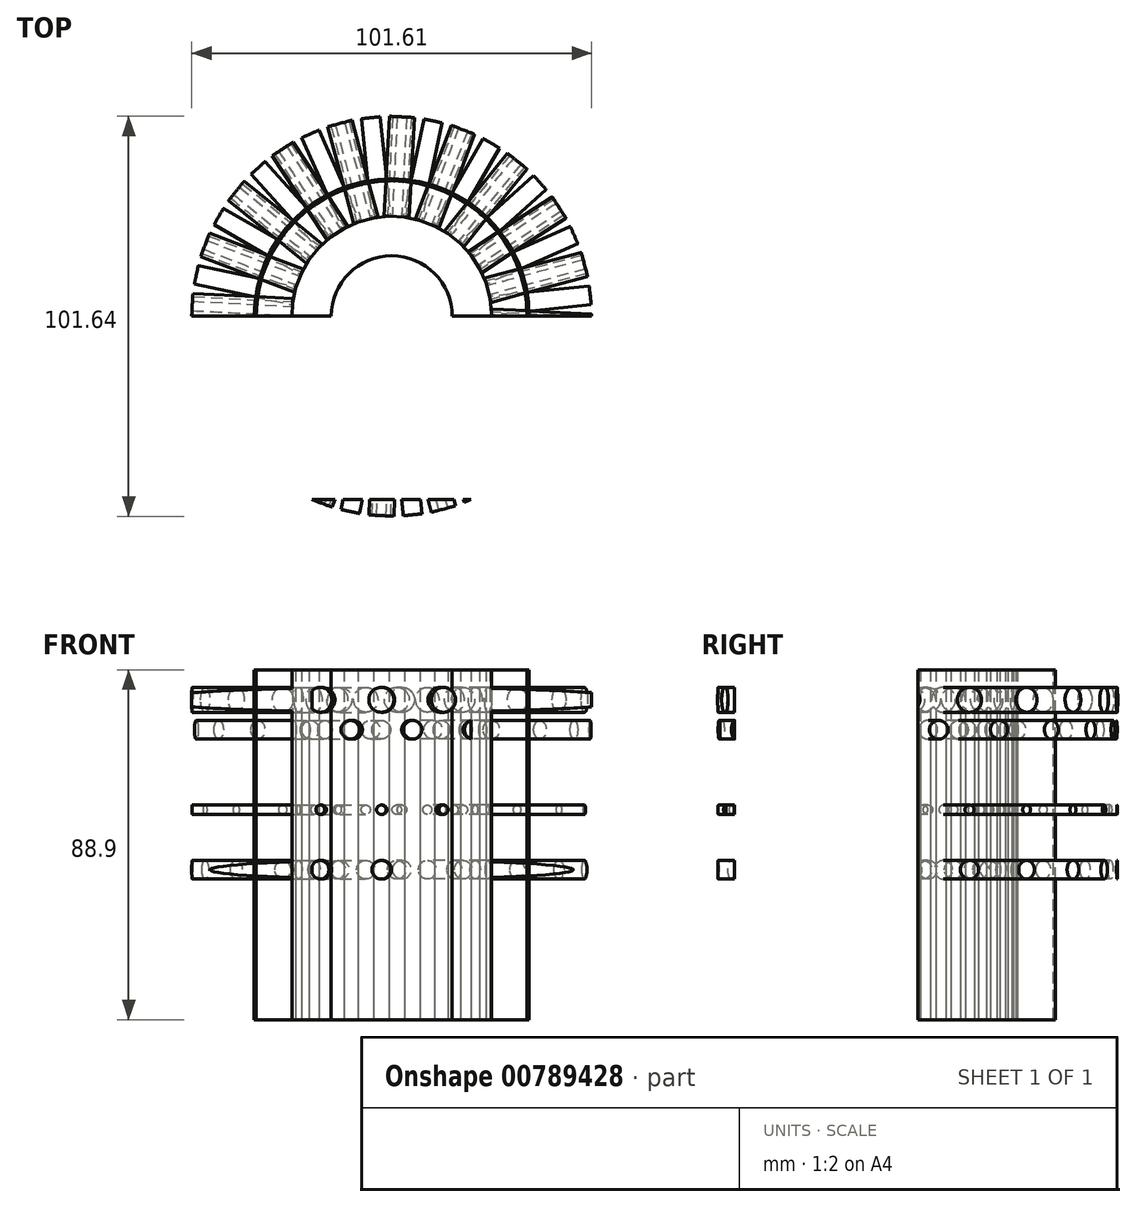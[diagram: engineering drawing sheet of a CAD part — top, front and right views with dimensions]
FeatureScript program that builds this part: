
annotation { "Feature Type Name" : "Feature", "Feature Type Description" : "" }
export const myFeature = defineFeature(function(context is Context, id is Id, definition is map)
    precondition{}
    {
        {
            var Q0;
            Q0=qCreatedBy(makeId("Top.planeOp"),FACE);
            var sketch = newSketch(context, id + "F0", { "sketchPlane" : qUnion([Q0])});
            skCircle(sketch, "E0.cCircle", {"center": v(0, 0) * mm, "radius": 25.32 * mm, "construction": true});
            skLineSegment(sketch, "E0.0", {"start": v(22.93, -10.92) * mm, "end": v(20.94, -14.37) * mm});
            skLineSegment(sketch, "E0.1", {"start": v(20.94, -14.37) * mm, "end": v(18.44, -17.47) * mm});
            skLineSegment(sketch, "E0.2", {"start": v(18.44, -17.47) * mm, "end": v(15.48, -20.14) * mm});
            skLineSegment(sketch, "E0.3", {"start": v(15.48, -20.14) * mm, "end": v(12.14, -22.31) * mm});
            skLineSegment(sketch, "E0.4", {"start": v(12.14, -22.31) * mm, "end": v(8.5, -23.94) * mm});
            skLineSegment(sketch, "E0.5", {"start": v(8.5, -23.94) * mm, "end": v(4.65, -24.97) * mm});
            skLineSegment(sketch, "E0.6", {"start": v(4.65, -24.97) * mm, "end": v(0.68, -25.4) * mm});
            skLineSegment(sketch, "E0.7", {"start": v(0.68, -25.4) * mm, "end": v(-3.3, -25.19) * mm});
            skLineSegment(sketch, "E0.8", {"start": v(-3.3, -25.19) * mm, "end": v(-7.2, -24.36) * mm});
            skLineSegment(sketch, "E0.9", {"start": v(-7.2, -24.36) * mm, "end": v(-10.92, -22.93) * mm});
            skLineSegment(sketch, "E0.10", {"start": v(-10.92, -22.93) * mm, "end": v(-14.37, -20.94) * mm});
            skLineSegment(sketch, "E0.11", {"start": v(-14.37, -20.94) * mm, "end": v(-17.47, -18.44) * mm});
            skLineSegment(sketch, "E0.12", {"start": v(-17.47, -18.44) * mm, "end": v(-20.14, -15.48) * mm});
            skLineSegment(sketch, "E0.13", {"start": v(-20.14, -15.48) * mm, "end": v(-22.31, -12.14) * mm});
            skLineSegment(sketch, "E0.14", {"start": v(-22.31, -12.14) * mm, "end": v(-23.94, -8.5) * mm});
            skLineSegment(sketch, "E0.15", {"start": v(-23.94, -8.5) * mm, "end": v(-24.97, -4.65) * mm});
            skLineSegment(sketch, "E0.16", {"start": v(-24.97, -4.65) * mm, "end": v(-25.4, -0.68) * mm});
            skLineSegment(sketch, "E0.17", {"start": v(-25.4, -0.68) * mm, "end": v(-25.19, 3.3) * mm});
            skLineSegment(sketch, "E0.18", {"start": v(-25.19, 3.3) * mm, "end": v(-24.36, 7.2) * mm});
            skLineSegment(sketch, "E0.19", {"start": v(-24.36, 7.2) * mm, "end": v(-22.93, 10.92) * mm});
            skLineSegment(sketch, "E0.20", {"start": v(-22.93, 10.92) * mm, "end": v(-20.94, 14.37) * mm});
            skLineSegment(sketch, "E0.21", {"start": v(-20.94, 14.37) * mm, "end": v(-18.44, 17.47) * mm});
            skLineSegment(sketch, "E0.22", {"start": v(-18.44, 17.47) * mm, "end": v(-15.48, 20.14) * mm});
            skLineSegment(sketch, "E0.23", {"start": v(-15.48, 20.14) * mm, "end": v(-12.14, 22.31) * mm});
            skLineSegment(sketch, "E0.24", {"start": v(-12.14, 22.31) * mm, "end": v(-8.5, 23.94) * mm});
            skLineSegment(sketch, "E0.25", {"start": v(-8.5, 23.94) * mm, "end": v(-4.65, 24.97) * mm});
            skLineSegment(sketch, "E0.26", {"start": v(-4.65, 24.97) * mm, "end": v(-0.68, 25.4) * mm});
            skLineSegment(sketch, "E0.27", {"start": v(-0.68, 25.4) * mm, "end": v(3.3, 25.19) * mm});
            skLineSegment(sketch, "E0.28", {"start": v(3.3, 25.19) * mm, "end": v(7.2, 24.36) * mm});
            skLineSegment(sketch, "E0.29", {"start": v(7.2, 24.36) * mm, "end": v(10.92, 22.93) * mm});
            skLineSegment(sketch, "E0.30", {"start": v(10.92, 22.93) * mm, "end": v(14.37, 20.94) * mm});
            skLineSegment(sketch, "E0.31", {"start": v(14.37, 20.94) * mm, "end": v(17.47, 18.44) * mm});
            skLineSegment(sketch, "E0.32", {"start": v(17.47, 18.44) * mm, "end": v(20.14, 15.48) * mm});
            skLineSegment(sketch, "E0.33", {"start": v(20.14, 15.48) * mm, "end": v(22.31, 12.14) * mm});
            skLineSegment(sketch, "E0.34", {"start": v(22.31, 12.14) * mm, "end": v(23.94, 8.5) * mm});
            skLineSegment(sketch, "E0.35", {"start": v(23.94, 8.5) * mm, "end": v(24.97, 4.65) * mm});
            skLineSegment(sketch, "E0.36", {"start": v(24.97, 4.65) * mm, "end": v(25.4, 0.68) * mm});
            skLineSegment(sketch, "E0.37", {"start": v(25.4, 0.68) * mm, "end": v(25.19, -3.3) * mm});
            skLineSegment(sketch, "E0.38", {"start": v(25.19, -3.3) * mm, "end": v(24.36, -7.2) * mm});
            skLineSegment(sketch, "E0.39", {"start": v(24.36, -7.2) * mm, "end": v(22.93, -10.92) * mm});
            skPoint(sketch, "E0.0.midPoint", {"position": v(21.94, -12.64) * mm});
            skCircle(sketch, "E1", {"center": v(0, 0) * mm, "radius": 15.37 * mm});
            skSolve(sketch);
        }
        {
            var Q0;
            Q0 = qSketchRegion(id + "F0", true);
            extrude(context, id + "F1", {"entities" : qUnion([Q0]), "depth" : 88.9 * mm, "offsetDistance" : 25.4 * mm});
        }
        {
            var Q0;
            Q0=makeQuery(id+"F1.opExtrude","SWEPT_FACE",FACE,{"disambiguationData":[OSD([sQuery(id+"F0.wireOp",EDGE,"E0.7")])]});
            var sketch = newSketch(context, id + "F2", { "sketchPlane" : qUnion([Q0])});
            skCircle(sketch, "E2", {"center": v(0, 81.28) * mm, "radius": 3.18 * mm});
            skPoint(sketch, "E2.centerSnap0", {"position": v(0, 88.9) * mm});
            skSolve(sketch);
        }
        {
            var Q0;
            Q0 = qSketchRegion(id + "F2", true);
            extrude(context, id + "F3", {"entities" : qUnion([Q0]), "depth" : 25.4 * mm, "offsetDistance" : 25.4 * mm});
        }
        {
            var Q0;
            Q0=makeQuery(id+"F3.opExtrude","SWEPT_BODY",BODY,{"disambiguationData":[OSD([sQuery(id+"F2.wireOp",EDGE,"E2")])]});
            var Q1;
            Q1=makeQuery(id+"F1.opExtrude","CAP_EDGE",EDGE,{"disambiguationData":[OSD([sQuery(id+"F0.wireOp",EDGE,"E1")])],"isStart":false});
            circularPattern(context, id + "F4", {"entities" : qUnion([Q0]), "axis" : qUnion([Q1]), "angle" : 360 * degree, "instanceCount" : 20, "equalSpace" : true});
        }
        {
            var Q0;
            Q0=makeQuery(id+"F4.opPattern","COPY",BODY,{"derivedFrom":makeQuery(id+"F3.opExtrude","SWEPT_BODY",BODY,{"disambiguationData":[OSD([sQuery(id+"F2.wireOp",EDGE,"E2")])]}),"instanceName":"10"});
            var Q1;
            Q1=makeQuery(id+"F4.opPattern","COPY",BODY,{"derivedFrom":makeQuery(id+"F3.opExtrude","SWEPT_BODY",BODY,{"disambiguationData":[OSD([sQuery(id+"F2.wireOp",EDGE,"E2")])]}),"instanceName":"11"});
            var Q2;
            Q2=makeQuery(id+"F4.opPattern","COPY",BODY,{"derivedFrom":makeQuery(id+"F3.opExtrude","SWEPT_BODY",BODY,{"disambiguationData":[OSD([sQuery(id+"F2.wireOp",EDGE,"E2")])]}),"instanceName":"12"});
            var Q3;
            Q3=makeQuery(id+"F4.opPattern","COPY",BODY,{"derivedFrom":makeQuery(id+"F3.opExtrude","SWEPT_BODY",BODY,{"disambiguationData":[OSD([sQuery(id+"F2.wireOp",EDGE,"E2")])]}),"instanceName":"13"});
            var Q4;
            Q4=makeQuery(id+"F4.opPattern","COPY",BODY,{"derivedFrom":makeQuery(id+"F3.opExtrude","SWEPT_BODY",BODY,{"disambiguationData":[OSD([sQuery(id+"F2.wireOp",EDGE,"E2")])]}),"instanceName":"14"});
            var Q5;
            Q5=makeQuery(id+"F4.opPattern","COPY",BODY,{"derivedFrom":makeQuery(id+"F3.opExtrude","SWEPT_BODY",BODY,{"disambiguationData":[OSD([sQuery(id+"F2.wireOp",EDGE,"E2")])]}),"instanceName":"15"});
            var Q6;
            Q6=makeQuery(id+"F4.opPattern","COPY",BODY,{"derivedFrom":makeQuery(id+"F3.opExtrude","SWEPT_BODY",BODY,{"disambiguationData":[OSD([sQuery(id+"F2.wireOp",EDGE,"E2")])]}),"instanceName":"16"});
            var Q7;
            Q7=makeQuery(id+"F4.opPattern","COPY",BODY,{"derivedFrom":makeQuery(id+"F3.opExtrude","SWEPT_BODY",BODY,{"disambiguationData":[OSD([sQuery(id+"F2.wireOp",EDGE,"E2")])]}),"instanceName":"17"});
            var Q8;
            Q8=makeQuery(id+"F4.opPattern","COPY",BODY,{"derivedFrom":makeQuery(id+"F3.opExtrude","SWEPT_BODY",BODY,{"disambiguationData":[OSD([sQuery(id+"F2.wireOp",EDGE,"E2")])]}),"instanceName":"18"});
            var Q9;
            Q9=makeQuery(id+"F4.opPattern","COPY",BODY,{"derivedFrom":makeQuery(id+"F3.opExtrude","SWEPT_BODY",BODY,{"disambiguationData":[OSD([sQuery(id+"F2.wireOp",EDGE,"E2")])]}),"instanceName":"19"});
            var Q10;
            Q10=makeQuery(id+"F3.opExtrude","SWEPT_BODY",BODY,{"disambiguationData":[OSD([sQuery(id+"F2.wireOp",EDGE,"E2")])]});
            var Q11;
            Q11=makeQuery(id+"F4.opPattern","COPY",BODY,{"derivedFrom":makeQuery(id+"F3.opExtrude","SWEPT_BODY",BODY,{"disambiguationData":[OSD([sQuery(id+"F2.wireOp",EDGE,"E2")])]}),"instanceName":"1"});
            var Q12;
            Q12=makeQuery(id+"F4.opPattern","COPY",BODY,{"derivedFrom":makeQuery(id+"F3.opExtrude","SWEPT_BODY",BODY,{"disambiguationData":[OSD([sQuery(id+"F2.wireOp",EDGE,"E2")])]}),"instanceName":"2"});
            var Q13;
            Q13=makeQuery(id+"F4.opPattern","COPY",BODY,{"derivedFrom":makeQuery(id+"F3.opExtrude","SWEPT_BODY",BODY,{"disambiguationData":[OSD([sQuery(id+"F2.wireOp",EDGE,"E2")])]}),"instanceName":"3"});
            var Q14;
            Q14=makeQuery(id+"F4.opPattern","COPY",BODY,{"derivedFrom":makeQuery(id+"F3.opExtrude","SWEPT_BODY",BODY,{"disambiguationData":[OSD([sQuery(id+"F2.wireOp",EDGE,"E2")])]}),"instanceName":"4"});
            var Q15;
            Q15=makeQuery(id+"F4.opPattern","COPY",BODY,{"derivedFrom":makeQuery(id+"F3.opExtrude","SWEPT_BODY",BODY,{"disambiguationData":[OSD([sQuery(id+"F2.wireOp",EDGE,"E2")])]}),"instanceName":"5"});
            var Q16;
            Q16=makeQuery(id+"F4.opPattern","COPY",BODY,{"derivedFrom":makeQuery(id+"F3.opExtrude","SWEPT_BODY",BODY,{"disambiguationData":[OSD([sQuery(id+"F2.wireOp",EDGE,"E2")])]}),"instanceName":"6"});
            var Q17;
            Q17=makeQuery(id+"F4.opPattern","COPY",BODY,{"derivedFrom":makeQuery(id+"F3.opExtrude","SWEPT_BODY",BODY,{"disambiguationData":[OSD([sQuery(id+"F2.wireOp",EDGE,"E2")])]}),"instanceName":"7"});
            var Q18;
            Q18=makeQuery(id+"F4.opPattern","COPY",BODY,{"derivedFrom":makeQuery(id+"F3.opExtrude","SWEPT_BODY",BODY,{"disambiguationData":[OSD([sQuery(id+"F2.wireOp",EDGE,"E2")])]}),"instanceName":"8"});
            var Q19;
            Q19=makeQuery(id+"F4.opPattern","COPY",BODY,{"derivedFrom":makeQuery(id+"F3.opExtrude","SWEPT_BODY",BODY,{"disambiguationData":[OSD([sQuery(id+"F2.wireOp",EDGE,"E2")])]}),"instanceName":"9"});
            var Q20;
            Q20=makeQuery(id+"F1.opExtrude","SWEPT_BODY",BODY,{"disambiguationData":[OSD([sQuery(id+"F0.wireOp",EDGE,"E0.0"),sQuery(id+"F0.wireOp",EDGE,"E0.1"),sQuery(id+"F0.wireOp",EDGE,"E0.2"),sQuery(id+"F0.wireOp",EDGE,"E0.3"),sQuery(id+"F0.wireOp",EDGE,"E0.4"),sQuery(id+"F0.wireOp",EDGE,"E0.5"),sQuery(id+"F0.wireOp",EDGE,"E0.6"),sQuery(id+"F0.wireOp",EDGE,"E0.7"),sQuery(id+"F0.wireOp",EDGE,"E0.8"),sQuery(id+"F0.wireOp",EDGE,"E0.9"),sQuery(id+"F0.wireOp",EDGE,"E0.10"),sQuery(id+"F0.wireOp",EDGE,"E0.11"),sQuery(id+"F0.wireOp",EDGE,"E0.12"),sQuery(id+"F0.wireOp",EDGE,"E0.13"),sQuery(id+"F0.wireOp",EDGE,"E0.14"),sQuery(id+"F0.wireOp",EDGE,"E0.15"),sQuery(id+"F0.wireOp",EDGE,"E0.16"),sQuery(id+"F0.wireOp",EDGE,"E0.17"),sQuery(id+"F0.wireOp",EDGE,"E0.18"),sQuery(id+"F0.wireOp",EDGE,"E0.19"),sQuery(id+"F0.wireOp",EDGE,"E0.20"),sQuery(id+"F0.wireOp",EDGE,"E0.21"),sQuery(id+"F0.wireOp",EDGE,"E0.22"),sQuery(id+"F0.wireOp",EDGE,"E0.23"),sQuery(id+"F0.wireOp",EDGE,"E0.24"),sQuery(id+"F0.wireOp",EDGE,"E0.25"),sQuery(id+"F0.wireOp",EDGE,"E0.26"),sQuery(id+"F0.wireOp",EDGE,"E0.27"),sQuery(id+"F0.wireOp",EDGE,"E0.28"),sQuery(id+"F0.wireOp",EDGE,"E0.29"),sQuery(id+"F0.wireOp",EDGE,"E0.30"),sQuery(id+"F0.wireOp",EDGE,"E0.31"),sQuery(id+"F0.wireOp",EDGE,"E0.32"),sQuery(id+"F0.wireOp",EDGE,"E0.33"),sQuery(id+"F0.wireOp",EDGE,"E0.34"),sQuery(id+"F0.wireOp",EDGE,"E0.35"),sQuery(id+"F0.wireOp",EDGE,"E0.36"),sQuery(id+"F0.wireOp",EDGE,"E0.37"),sQuery(id+"F0.wireOp",EDGE,"E0.38"),sQuery(id+"F0.wireOp",EDGE,"E0.39"),sQuery(id+"F0.wireOp",EDGE,"E1")])]});
            booleanBodies(context, id + "F5", {"operationType" : BooleanOperationType.UNION, "tools" : qUnion([Q0, Q1, Q2, Q3, Q4, Q5, Q6, Q7, Q8, Q9, Q10, Q11, Q12, Q13, Q14, Q15, Q16, Q17, Q18, Q19, Q20])});
        }
        {
            var Q0;
            Q0=makeQuery(id+"F1.opExtrude","SWEPT_FACE",FACE,{"disambiguationData":[OSD([sQuery(id+"F0.wireOp",EDGE,"E0.6")])]});
            var sketch = newSketch(context, id + "F6", { "sketchPlane" : qUnion([Q0])});
            skCircle(sketch, "E3", {"center": v(0, 73.66) * mm, "radius": 2.38 * mm});
            skSolve(sketch);
        }
        {
            var Q0;
            Q0 = qSketchRegion(id + "F6", true);
            extrude(context, id + "F7", {"entities" : qUnion([Q0]), "operationType" : NewBodyOperationType.ADD, "depth" : 25.4 * mm, "offsetDistance" : 25.4 * mm});
        }
        {
            var Q0;
            Q0=makeQuery(id+"F4.opPattern","COPY",BODY,{"derivedFrom":makeQuery(id+"F3.opExtrude","SWEPT_BODY",BODY,{"disambiguationData":[OSD([sQuery(id+"F2.wireOp",EDGE,"E2")])]}),"instanceName":"10"});
            var Q1;
            Q1=makeQuery(id+"F1.opExtrude","CAP_EDGE",EDGE,{"disambiguationData":[OSD([sQuery(id+"F0.wireOp",EDGE,"E1")])],"isStart":false});
            circularPattern(context, id + "F8", {"entities" : qUnion([Q0]), "axis" : qUnion([Q1]), "angle" : 360 * degree, "instanceCount" : 20, "equalSpace" : true});
        }
        {
            var Q0;
            {var subQ1=sQuery(id+"F0.wireOp",EDGE,"E0.10");var subQ2=sQuery(id+"F0.wireOp",EDGE,"E0.9");var subQ3=sQuery(id+"F0.wireOp",EDGE,"E0.8");Q0=makeQuery(id+"F8.opPattern","COPY",FACE,{"derivedFrom":makeQuery(id+"F5.opBoolean","SPLIT",FACE,{"disambiguationData":[TD([makeQuery(id+"F1.opExtrude","CAP_FACE",FACE,{"disambiguationData":[OSD([sQuery(id+"F0.wireOp",EDGE,"E0.0"),sQuery(id+"F0.wireOp",EDGE,"E0.1"),sQuery(id+"F0.wireOp",EDGE,"E0.2"),sQuery(id+"F0.wireOp",EDGE,"E0.3"),sQuery(id+"F0.wireOp",EDGE,"E0.4"),sQuery(id+"F0.wireOp",EDGE,"E0.5"),sQuery(id+"F0.wireOp",EDGE,"E0.6"),sQuery(id+"F0.wireOp",EDGE,"E0.7"),subQ3,subQ2,subQ1,sQuery(id+"F0.wireOp",EDGE,"E0.11"),sQuery(id+"F0.wireOp",EDGE,"E0.12"),sQuery(id+"F0.wireOp",EDGE,"E0.13"),sQuery(id+"F0.wireOp",EDGE,"E0.14"),sQuery(id+"F0.wireOp",EDGE,"E0.15"),sQuery(id+"F0.wireOp",EDGE,"E0.16"),sQuery(id+"F0.wireOp",EDGE,"E0.17"),sQuery(id+"F0.wireOp",EDGE,"E0.18"),sQuery(id+"F0.wireOp",EDGE,"E0.19"),sQuery(id+"F0.wireOp",EDGE,"E0.20"),sQuery(id+"F0.wireOp",EDGE,"E0.21"),sQuery(id+"F0.wireOp",EDGE,"E0.22"),sQuery(id+"F0.wireOp",EDGE,"E0.23"),sQuery(id+"F0.wireOp",EDGE,"E0.24"),sQuery(id+"F0.wireOp",EDGE,"E0.25"),sQuery(id+"F0.wireOp",EDGE,"E0.26"),sQuery(id+"F0.wireOp",EDGE,"E0.27"),sQuery(id+"F0.wireOp",EDGE,"E0.28"),sQuery(id+"F0.wireOp",EDGE,"E0.29"),sQuery(id+"F0.wireOp",EDGE,"E0.30"),sQuery(id+"F0.wireOp",EDGE,"E0.31"),sQuery(id+"F0.wireOp",EDGE,"E0.32"),sQuery(id+"F0.wireOp",EDGE,"E0.33"),sQuery(id+"F0.wireOp",EDGE,"E0.34"),sQuery(id+"F0.wireOp",EDGE,"E0.35"),sQuery(id+"F0.wireOp",EDGE,"E0.36"),sQuery(id+"F0.wireOp",EDGE,"E0.37"),sQuery(id+"F0.wireOp",EDGE,"E0.38"),sQuery(id+"F0.wireOp",EDGE,"E0.39"),sQuery(id+"F0.wireOp",EDGE,"E1")])],"isStart":true})])],"derivedFrom":makeQuery(id+"F1.opExtrude","SWEPT_FACE",FACE,{"disambiguationData":[OSD([subQ2])]})}),"instanceName":"1"});}
            var sketch = newSketch(context, id + "F9", { "sketchPlane" : qUnion([Q0])});
            skCircle(sketch, "E4", {"center": v(0, 53.34) * mm, "radius": 1.2 * mm});
            skSolve(sketch);
        }
        {
            var Q0;
            Q0 = qSketchRegion(id + "F9", true);
            extrude(context, id + "F10", {"entities" : qUnion([Q0]), "depth" : 25.4 * mm, "offsetDistance" : 25.4 * mm});
        }
        {
            var Q0;
            Q0=makeQuery(id+"F10.opExtrude","SWEPT_BODY",BODY,{"disambiguationData":[OSD([sQuery(id+"F9.wireOp",EDGE,"E4")])]});
            var Q1;
            Q1=makeQuery(id+"F8.opPattern","COPY",EDGE,{"derivedFrom":makeQuery(id+"F1.opExtrude","CAP_EDGE",EDGE,{"disambiguationData":[OSD([sQuery(id+"F0.wireOp",EDGE,"E1")])],"isStart":true}),"instanceName":"1"});
            circularPattern(context, id + "F11", {"entities" : qUnion([Q0]), "axis" : qUnion([Q1]), "angle" : 360 * degree, "instanceCount" : 20, "equalSpace" : true});
        }
        {
            var Q0;
            {var subQ1=sQuery(id+"F0.wireOp",EDGE,"E0.10");var subQ2=sQuery(id+"F0.wireOp",EDGE,"E0.9");var subQ3=sQuery(id+"F0.wireOp",EDGE,"E0.8");Q0=makeQuery(id+"F8.opPattern","COPY",FACE,{"derivedFrom":makeQuery(id+"F5.opBoolean","SPLIT",FACE,{"disambiguationData":[TD([makeQuery(id+"F1.opExtrude","CAP_FACE",FACE,{"disambiguationData":[OSD([sQuery(id+"F0.wireOp",EDGE,"E0.0"),sQuery(id+"F0.wireOp",EDGE,"E0.1"),sQuery(id+"F0.wireOp",EDGE,"E0.2"),sQuery(id+"F0.wireOp",EDGE,"E0.3"),sQuery(id+"F0.wireOp",EDGE,"E0.4"),sQuery(id+"F0.wireOp",EDGE,"E0.5"),sQuery(id+"F0.wireOp",EDGE,"E0.6"),sQuery(id+"F0.wireOp",EDGE,"E0.7"),subQ3,subQ2,subQ1,sQuery(id+"F0.wireOp",EDGE,"E0.11"),sQuery(id+"F0.wireOp",EDGE,"E0.12"),sQuery(id+"F0.wireOp",EDGE,"E0.13"),sQuery(id+"F0.wireOp",EDGE,"E0.14"),sQuery(id+"F0.wireOp",EDGE,"E0.15"),sQuery(id+"F0.wireOp",EDGE,"E0.16"),sQuery(id+"F0.wireOp",EDGE,"E0.17"),sQuery(id+"F0.wireOp",EDGE,"E0.18"),sQuery(id+"F0.wireOp",EDGE,"E0.19"),sQuery(id+"F0.wireOp",EDGE,"E0.20"),sQuery(id+"F0.wireOp",EDGE,"E0.21"),sQuery(id+"F0.wireOp",EDGE,"E0.22"),sQuery(id+"F0.wireOp",EDGE,"E0.23"),sQuery(id+"F0.wireOp",EDGE,"E0.24"),sQuery(id+"F0.wireOp",EDGE,"E0.25"),sQuery(id+"F0.wireOp",EDGE,"E0.26"),sQuery(id+"F0.wireOp",EDGE,"E0.27"),sQuery(id+"F0.wireOp",EDGE,"E0.28"),sQuery(id+"F0.wireOp",EDGE,"E0.29"),sQuery(id+"F0.wireOp",EDGE,"E0.30"),sQuery(id+"F0.wireOp",EDGE,"E0.31"),sQuery(id+"F0.wireOp",EDGE,"E0.32"),sQuery(id+"F0.wireOp",EDGE,"E0.33"),sQuery(id+"F0.wireOp",EDGE,"E0.34"),sQuery(id+"F0.wireOp",EDGE,"E0.35"),sQuery(id+"F0.wireOp",EDGE,"E0.36"),sQuery(id+"F0.wireOp",EDGE,"E0.37"),sQuery(id+"F0.wireOp",EDGE,"E0.38"),sQuery(id+"F0.wireOp",EDGE,"E0.39"),sQuery(id+"F0.wireOp",EDGE,"E1")])],"isStart":true})])],"derivedFrom":makeQuery(id+"F1.opExtrude","SWEPT_FACE",FACE,{"disambiguationData":[OSD([subQ2])]})}),"instanceName":"1"});}
            var sketch = newSketch(context, id + "F12", { "sketchPlane" : qUnion([Q0])});
            skCircle(sketch, "E5", {"center": v(0, 38.1) * mm, "radius": 2.38 * mm});
            skSolve(sketch);
        }
        {
            var Q0;
            Q0 = qSketchRegion(id + "F12", true);
            extrude(context, id + "F13", {"entities" : qUnion([Q0]), "depth" : 25.4 * mm, "offsetDistance" : 25.4 * mm});
        }
        {
            var Q0;
            Q0=makeQuery(id+"F13.opExtrude","SWEPT_BODY",BODY,{"disambiguationData":[OSD([sQuery(id+"F12.wireOp",EDGE,"E5")])]});
            var Q1;
            Q1=makeQuery(id+"F8.opPattern","COPY",EDGE,{"derivedFrom":makeQuery(id+"F1.opExtrude","CAP_EDGE",EDGE,{"disambiguationData":[OSD([sQuery(id+"F0.wireOp",EDGE,"E1")])],"isStart":true}),"instanceName":"1"});
            circularPattern(context, id + "F14", {"entities" : qUnion([Q0]), "axis" : qUnion([Q1]), "angle" : 360 * degree, "instanceCount" : 20, "equalSpace" : true});
        }
        {
            var Q0;
            Q0=makeQuery(id+"F8.opPattern","COPY",FACE,{"derivedFrom":makeQuery(id+"F1.opExtrude","CAP_FACE",FACE,{"disambiguationData":[OSD([sQuery(id+"F0.wireOp",EDGE,"E0.0"),sQuery(id+"F0.wireOp",EDGE,"E0.1"),sQuery(id+"F0.wireOp",EDGE,"E0.2"),sQuery(id+"F0.wireOp",EDGE,"E0.3"),sQuery(id+"F0.wireOp",EDGE,"E0.4"),sQuery(id+"F0.wireOp",EDGE,"E0.5"),sQuery(id+"F0.wireOp",EDGE,"E0.6"),sQuery(id+"F0.wireOp",EDGE,"E0.7"),sQuery(id+"F0.wireOp",EDGE,"E0.8"),sQuery(id+"F0.wireOp",EDGE,"E0.9"),sQuery(id+"F0.wireOp",EDGE,"E0.10"),sQuery(id+"F0.wireOp",EDGE,"E0.11"),sQuery(id+"F0.wireOp",EDGE,"E0.12"),sQuery(id+"F0.wireOp",EDGE,"E0.13"),sQuery(id+"F0.wireOp",EDGE,"E0.14"),sQuery(id+"F0.wireOp",EDGE,"E0.15"),sQuery(id+"F0.wireOp",EDGE,"E0.16"),sQuery(id+"F0.wireOp",EDGE,"E0.17"),sQuery(id+"F0.wireOp",EDGE,"E0.18"),sQuery(id+"F0.wireOp",EDGE,"E0.19"),sQuery(id+"F0.wireOp",EDGE,"E0.20"),sQuery(id+"F0.wireOp",EDGE,"E0.21"),sQuery(id+"F0.wireOp",EDGE,"E0.22"),sQuery(id+"F0.wireOp",EDGE,"E0.23"),sQuery(id+"F0.wireOp",EDGE,"E0.24"),sQuery(id+"F0.wireOp",EDGE,"E0.25"),sQuery(id+"F0.wireOp",EDGE,"E0.26"),sQuery(id+"F0.wireOp",EDGE,"E0.27"),sQuery(id+"F0.wireOp",EDGE,"E0.28"),sQuery(id+"F0.wireOp",EDGE,"E0.29"),sQuery(id+"F0.wireOp",EDGE,"E0.30"),sQuery(id+"F0.wireOp",EDGE,"E0.31"),sQuery(id+"F0.wireOp",EDGE,"E0.32"),sQuery(id+"F0.wireOp",EDGE,"E0.33"),sQuery(id+"F0.wireOp",EDGE,"E0.34"),sQuery(id+"F0.wireOp",EDGE,"E0.35"),sQuery(id+"F0.wireOp",EDGE,"E0.36"),sQuery(id+"F0.wireOp",EDGE,"E0.37"),sQuery(id+"F0.wireOp",EDGE,"E0.38"),sQuery(id+"F0.wireOp",EDGE,"E0.39"),sQuery(id+"F0.wireOp",EDGE,"E1")])],"isStart":false}),"instanceName":"1"});
            var sketch = newSketch(context, id + "F15", { "sketchPlane" : qUnion([Q0])});
            skCircle(sketch, "E6", {"center": v(0, 0) * mm, "radius": 34.93 * mm});
            skCircle(sketch, "E7", {"center": v(0, 0) * mm, "radius": 34.42 * mm});
            skSolve(sketch);
        }
        {
            var Q0;
            Q0 = qSketchRegion(id + "F15", true);
            extrude(context, id + "F16", {"entities" : qUnion([Q0]), "oppositeDirection" : true, "depth" : 88.9 * mm, "offsetDistance" : 25.4 * mm});
        }
        {
            var Q0;
            Q0=makeQuery(id+"F14.opPattern","COPY",BODY,{"derivedFrom":makeQuery(id+"F13.opExtrude","SWEPT_BODY",BODY,{"disambiguationData":[OSD([sQuery(id+"F12.wireOp",EDGE,"E5")])]}),"instanceName":"1"});
            var Q1;
            Q1=makeQuery(id+"F16.opExtrude","SWEPT_BODY",BODY,{"disambiguationData":[OSD([sQuery(id+"F15.wireOp",EDGE,"E6"),sQuery(id+"F15.wireOp",EDGE,"E7")])]});
            booleanBodies(context, id + "F17", {"operationType" : BooleanOperationType.SUBTRACTION, "tools" : qUnion([Q0]), "targets" : qUnion([Q1])});
        }
        {
            var Q0;
            Q0=qCreatedBy(makeId("Top.planeOp"),FACE);
            var sketch = newSketch(context, id + "F18", { "sketchPlane" : qUnion([Q0])});
            skLineSegment(sketch, "E8.bottom", {"start": v(-55.46, 0) * mm, "end": v(61.9, 0) * mm});
            skLineSegment(sketch, "E8.top", {"start": v(-55.46, -46.55) * mm, "end": v(61.9, -46.55) * mm});
            skLineSegment(sketch, "E8.left", {"start": v(-55.46, 0) * mm, "end": v(-55.46, -46.55) * mm});
            skLineSegment(sketch, "E8.right", {"start": v(61.9, 0) * mm, "end": v(61.9, -46.55) * mm});
            skSolve(sketch);
        }
        {
            var Q0;
            Q0 = qSketchRegion(id + "F18", true);
            extrude(context, id + "F19", {"entities" : qUnion([Q0]), "operationType" : NewBodyOperationType.REMOVE, "endBound" : BoundingType.THROUGH_ALL, "depth" : 25.4 * mm, "offsetDistance" : 25.4 * mm});
        }
    });
